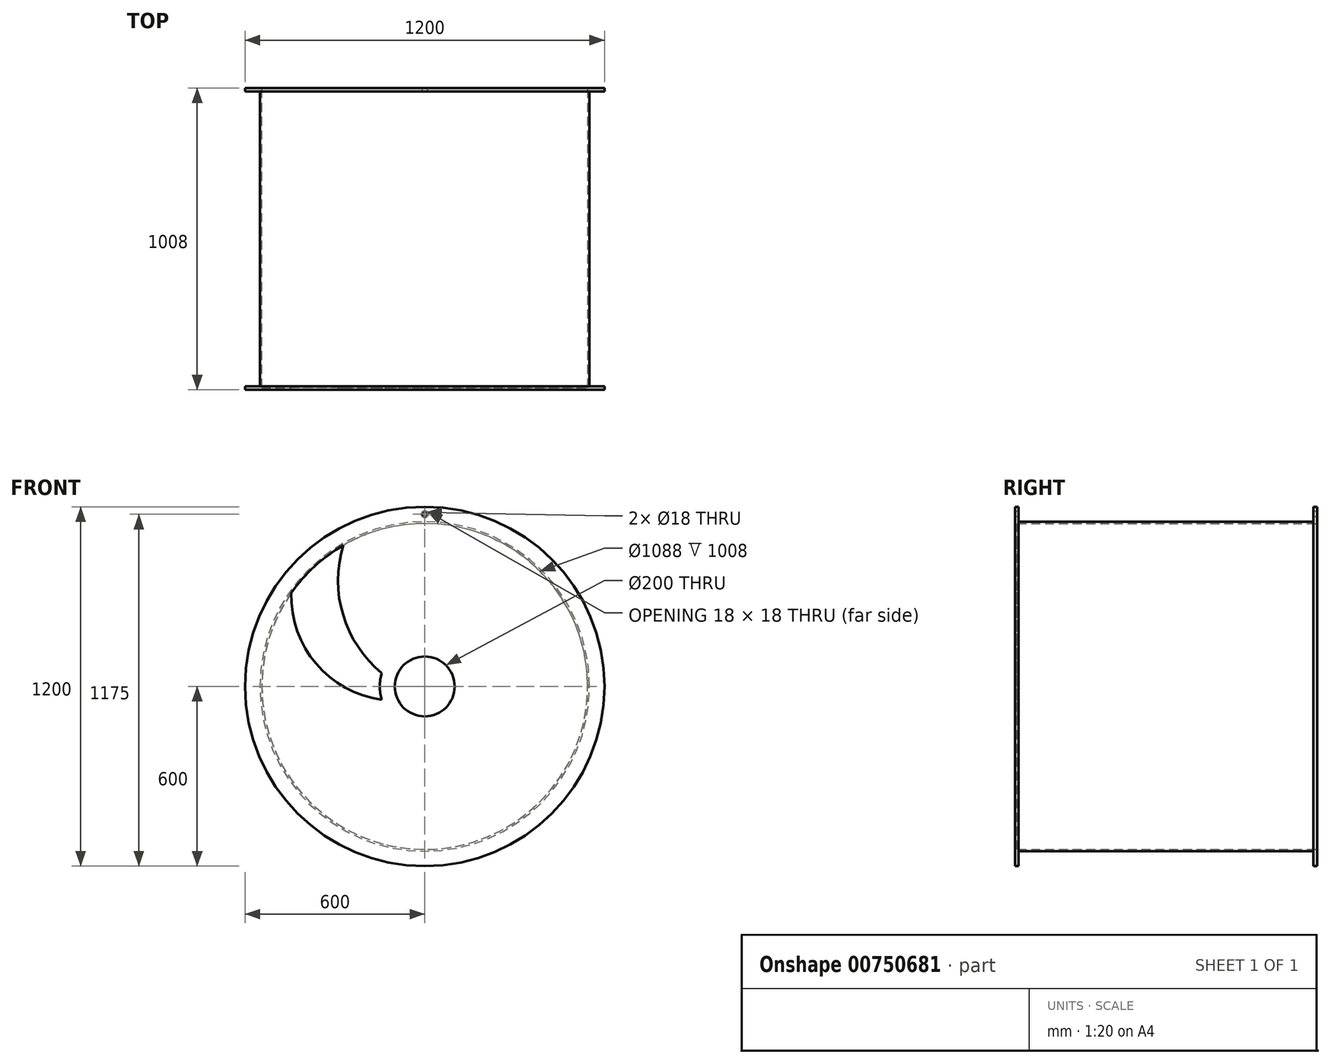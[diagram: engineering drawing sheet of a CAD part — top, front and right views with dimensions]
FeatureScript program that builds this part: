
annotation { "Feature Type Name" : "Feature", "Feature Type Description" : "" }
export const myFeature = defineFeature(function(context is Context, id is Id, definition is map)
    precondition{}
    {
        {
            var Q0;
            Q0=qCreatedBy(makeId("Right.planeOp"),FACE);
            var sketch = newSketch(context, id + "F0", { "sketchPlane" : qUnion([Q0])});
            skLineSegment(sketch, "E0", {"start": v(0, 600) * mm, "end": v(0, 0) * mm});
            skLineSegment(sketch, "E1", {"start": v(8, 0) * mm, "end": v(8, 544) * mm});
            skLineSegment(sketch, "E2", {"start": v(8, 544) * mm, "end": v(1008, 544) * mm});
            skLineSegment(sketch, "E3", {"start": v(1008, 544) * mm, "end": v(1008, 600) * mm});
            skLineSegment(sketch, "E4", {"start": v(996, 600) * mm, "end": v(996, 550) * mm});
            skLineSegment(sketch, "E5", {"start": v(996, 550) * mm, "end": v(12, 550) * mm});
            skLineSegment(sketch, "E6", {"start": v(12, 550) * mm, "end": v(12, 600) * mm});
            skLineSegment(sketch, "E7", {"start": v(0, 600) * mm, "end": v(12, 600) * mm});
            skLineSegment(sketch, "E8", {"start": v(1008, 600) * mm, "end": v(996, 600) * mm});
            skLineSegment(sketch, "E9", {"start": v(8, 0) * mm, "end": v(0, 0) * mm});
            skSolve(sketch);
        }
        {
            var Q0;
            Q0 = qSketchRegion(id + "F0", true);
            var Q1;
            Q1=sQuery(id+"F0.wireOp",EDGE,"E9");
            revolve(context, id + "F1", {"surfaceOperationType" : NewSurfaceOperationType.NEW, "entities" : qUnion([Q0]), "axis" : qUnion([Q1]), "revolveType" : RevolveType.FULL});
        }
        {
            var Q0;
            Q0=makeQuery(id+"F1.opRevolve","SWEPT_FACE",FACE,{"disambiguationData":[OSD([sQuery(id+"F0.wireOp",EDGE,"E0")])]});
            var sketch = newSketch(context, id + "F2", { "sketchPlane" : qUnion([Q0])});
            skCircle(sketch, "E10", {"center": v(0, 0) * mm, "radius": 100 * mm});
            skSolve(sketch);
        }
        {
            var Q0;
            Q0=makeQuery(id+"F2.imprint","IMPRINT",FACE,{"disambiguationData":[TD([[makeQuery(id+"F2.imprint","IMPRINT",EDGE,{"derivedFrom":sQuery(id+"F2.wireOp",EDGE,"E10")}),1.0]])]});
            var Q1;
            Q1=sQuery(id+"F2.wireOp",EDGE,"E10");
            var Q2;
            Q2 = qBodyType(qCreatedBy(id + "F2" ,EDGE), BodyType.WIRE);
            extrude(context, id + "F3", {"entities" : qUnion([Q0]), "operationType" : NewBodyOperationType.REMOVE, "surfaceEntities" : qUnion([Q1, Q2]), "oppositeDirection" : true, "depth" : 25 * mm, "offsetDistance" : 25 * mm});
        }
        {
            var Q0;
            Q0=makeQuery(id+"F1.opRevolve","SWEPT_FACE",FACE,{"disambiguationData":[OSD([sQuery(id+"F0.wireOp",EDGE,"E0")])]});
            var sketch = newSketch(context, id + "F4", { "sketchPlane" : qUnion([Q0])});
            skCircle(sketch, "E11", {"center": v(0, 575) * mm, "radius": 9 * mm});
            skSolve(sketch);
        }
        {
            var Q0;
            Q0=makeQuery(id+"F4.imprint","IMPRINT",FACE,{"disambiguationData":[TD([[makeQuery(id+"F4.imprint","IMPRINT",EDGE,{"derivedFrom":sQuery(id+"F4.wireOp",EDGE,"E11")}),1.0]])]});
            var Q1;
            Q1=sQuery(id+"F4.wireOp",EDGE,"E11");
            extrude(context, id + "F5", {"entities" : qUnion([Q0]), "operationType" : NewBodyOperationType.REMOVE, "surfaceEntities" : qUnion([Q1]), "endBound" : BoundingType.THROUGH_ALL, "oppositeDirection" : true, "depth" : 25 * mm, "offsetDistance" : 25 * mm});
        }
        {
            var Q0;
            Q0=makeQuery(id+"F1.opRevolve","SWEPT_FACE",FACE,{"disambiguationData":[OSD([sQuery(id+"F0.wireOp",EDGE,"E0")])]});
            var sketch = newSketch(context, id + "F6", { "sketchPlane" : qUnion([Q0])});
            skLineSegment(sketch, "E12", {"start": v(0, 0) * mm, "end": v(0, 516.92) * mm, "construction": true});
            skLineSegment(sketch, "E13", {"start": v(-272, 471.12) * mm, "end": v(0, 0) * mm, "construction": true});
            skArc(sketch, "E14", {"start": v(-272, 471.12) * mm, "mid": v(-367.52, 401.08) * mm, "end": v(-445.62, 312.03) * mm});
            skArc(sketch, "E15", {"start": v(-445.62, 312.03) * mm, "mid": v(-362.65, 75.97) * mm, "end": v(-143.29, -44.37) * mm});
            skArc(sketch, "E16", {"start": v(-143.29, -44.37) * mm, "mid": v(-150, 0) * mm, "end": v(-143.29, 44.37) * mm});
            skArc(sketch, "E17", {"start": v(-272, 471.12) * mm, "mid": v(-272.6, 238.15) * mm, "end": v(-143.29, 44.37) * mm});
            skLineSegment(sketch, "E18", {"start": v(-143.29, 44.37) * mm, "end": v(0, 0) * mm, "construction": true});
            skLineSegment(sketch, "E19", {"start": v(0, 0) * mm, "end": v(-143.29, -44.37) * mm, "construction": true});
            skLineSegment(sketch, "E20", {"start": v(-445.62, 312.03) * mm, "end": v(0, 0) * mm, "construction": true});
            skSolve(sketch);
        }
        {
            var Q0;
            Q0=makeQuery(id+"F6.imprint","IMPRINT",FACE,{"disambiguationData":[TD([[makeQuery(id+"F6.imprint","IMPRINT",EDGE,{"derivedFrom":sQuery(id+"F6.wireOp",EDGE,"E14")}),1.0]])]});
            extrude(context, id + "F7", {"entities" : qUnion([Q0]), "operationType" : NewBodyOperationType.REMOVE, "oppositeDirection" : true, "depth" : 25 * mm, "offsetDistance" : 25 * mm});
        }
    });
